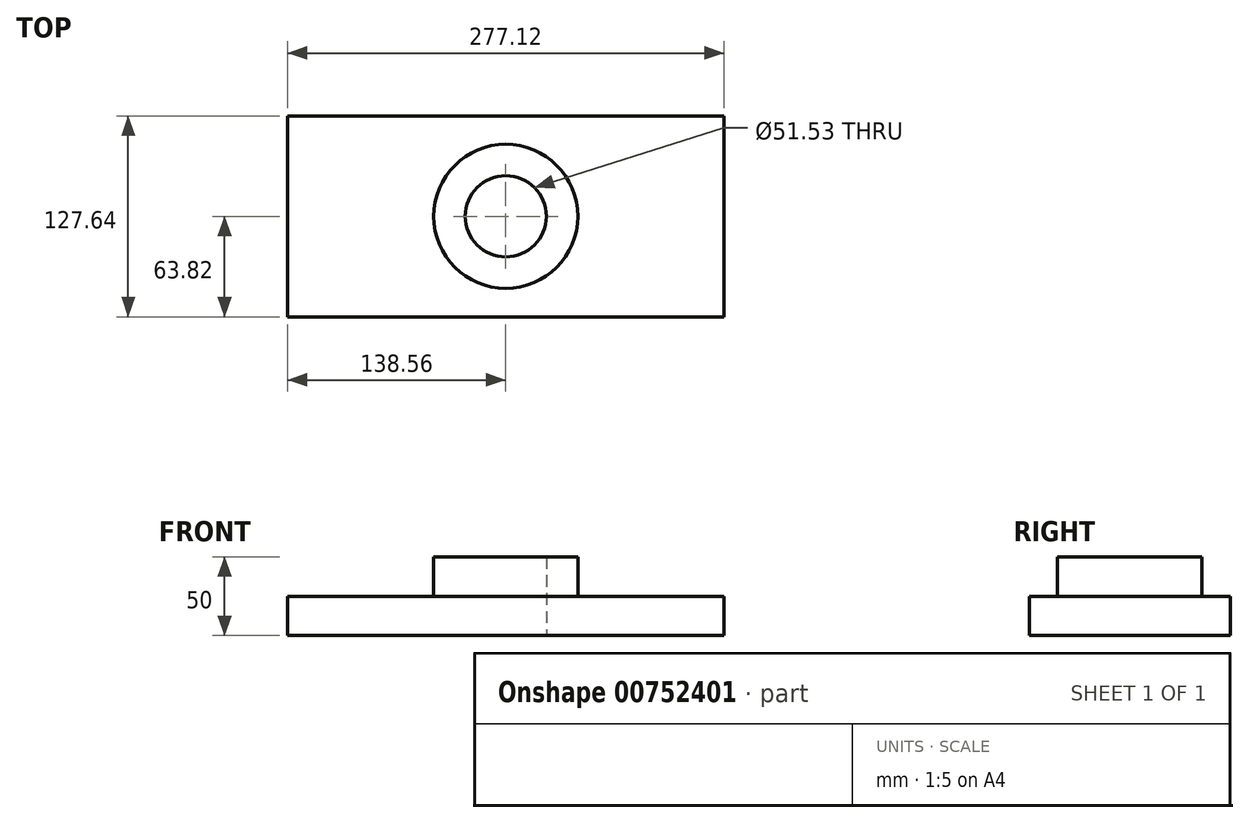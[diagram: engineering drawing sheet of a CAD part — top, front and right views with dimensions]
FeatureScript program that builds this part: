
annotation { "Feature Type Name" : "Feature", "Feature Type Description" : "" }
export const myFeature = defineFeature(function(context is Context, id is Id, definition is map)
    precondition{}
    {
        {
            var Q0;
            Q0=qCreatedBy(makeId("Top.planeOp"),FACE);
            var sketch = newSketch(context, id + "F0", { "sketchPlane" : qUnion([Q0])});
            skCircle(sketch, "E0", {"center": v(0, 0) * mm, "radius": 25.77 * mm});
            skLineSegment(sketch, "E1.bottom", {"start": v(138.56, 63.82) * mm, "end": v(-138.56, 63.82) * mm});
            skLineSegment(sketch, "E1.top", {"start": v(138.56, -63.82) * mm, "end": v(-138.56, -63.82) * mm});
            skLineSegment(sketch, "E1.left", {"start": v(138.56, 63.82) * mm, "end": v(138.56, -63.82) * mm});
            skLineSegment(sketch, "E1.right", {"start": v(-138.56, 63.82) * mm, "end": v(-138.56, -63.82) * mm});
            skSolve(sketch);
        }
        {
            var Q0;
            Q0=makeQuery(id+"F0.imprint","IMPRINT",FACE,{"disambiguationData":[TD([[makeQuery(id+"F0.imprint","IMPRINT",EDGE,{"derivedFrom":sQuery(id+"F0.wireOp",EDGE,"E0")}),-1.0]])]});
            extrude(context, id + "F1", {"entities" : qUnion([Q0]), "depth" : 25 * mm, "offsetDistance" : 25 * mm});
        }
        {
            var Q0;
            Q0=makeQuery(id+"F1.opExtrude","CAP_FACE",FACE,{"disambiguationData":[OSD([sQuery(id+"F0.wireOp",EDGE,"E0"),sQuery(id+"F0.wireOp",EDGE,"E1.bottom"),sQuery(id+"F0.wireOp",EDGE,"E1.top"),sQuery(id+"F0.wireOp",EDGE,"E1.left"),sQuery(id+"F0.wireOp",EDGE,"E1.right")])],"isStart":false});
            var sketch = newSketch(context, id + "F2", { "sketchPlane" : qUnion([Q0])});
            skCircle(sketch, "E2.0", {"center": v(0, 0) * mm, "radius": 45.77 * mm});
            skSolve(sketch);
        }
        {
            var Q0;
            Q0=makeQuery(id+"F2.imprint","IMPRINT",FACE,{"disambiguationData":[TD([[makeQuery(id+"F2.imprint","IMPRINT",EDGE,{"derivedFrom":sQuery(id+"F2.wireOp",EDGE,"E2.0")}),1.0]])]});
            extrude(context, id + "F3", {"entities" : qUnion([Q0]), "operationType" : NewBodyOperationType.ADD, "depth" : 25 * mm, "offsetDistance" : 25 * mm});
        }
    });
